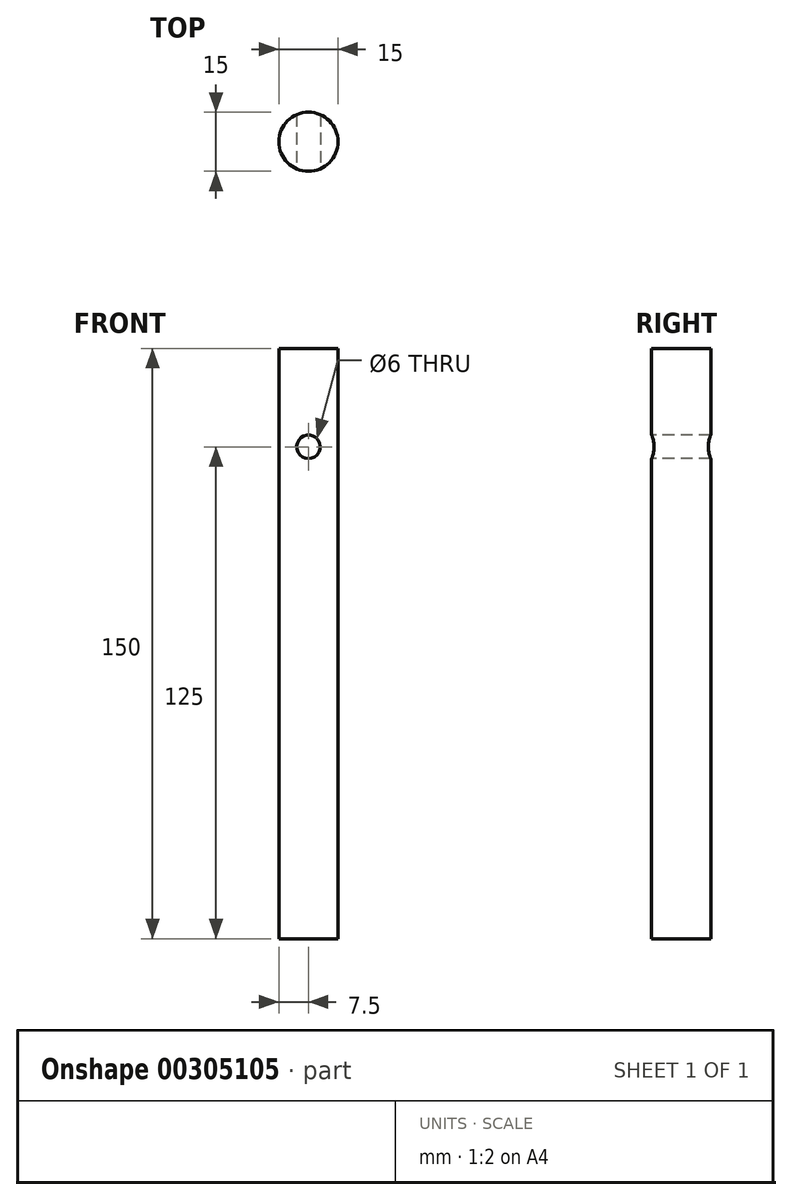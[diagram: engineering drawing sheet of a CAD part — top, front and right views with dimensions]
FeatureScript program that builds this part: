
annotation { "Feature Type Name" : "Feature", "Feature Type Description" : "" }
export const myFeature = defineFeature(function(context is Context, id is Id, definition is map)
    precondition{}
    {
        {
            var Q0;
            Q0=qCreatedBy(makeId("Top.planeOp"),FACE);
            var sketch = newSketch(context, id + "F0", { "sketchPlane" : qUnion([Q0])});
            skCircle(sketch, "E0", {"center": v(0, 0) * mm, "radius": 7.5 * mm});
            skSolve(sketch);
        }
        {
            var Q0;
            Q0=makeQuery(id+"F0.imprint","IMPRINT",FACE,{"disambiguationData":[TD([[makeQuery(id+"F0.imprint","IMPRINT",EDGE,{"derivedFrom":sQuery(id+"F0.wireOp",EDGE,"E0")}),1.0]])]});
            extrude(context, id + "F1", {"entities" : qUnion([Q0]), "depth" : 150 * mm, "symmetric" : true});
        }
        {
            var Q0;
            Q0=qCreatedBy(makeId("Front.planeOp"),FACE);
            var sketch = newSketch(context, id + "F2", { "sketchPlane" : qUnion([Q0])});
            skCircle(sketch, "E1", {"center": v(0, 50) * mm, "radius": 3 * mm});
            skSolve(sketch);
        }
        {
            var Q0;
            Q0 = qSketchRegion(id + "F2", true);
            extrude(context, id + "F3", {"entities" : qUnion([Q0]), "operationType" : NewBodyOperationType.REMOVE, "endBound" : BoundingType.THROUGH_ALL, "oppositeDirection" : true, "depth" : 25 * mm, "hasSecondDirection" : true, "secondDirectionBound" : BoundingType.THROUGH_ALL, "secondDirectionOppositeDirection" : false, "secondDirectionDepth" : 25 * mm});
        }
    });
